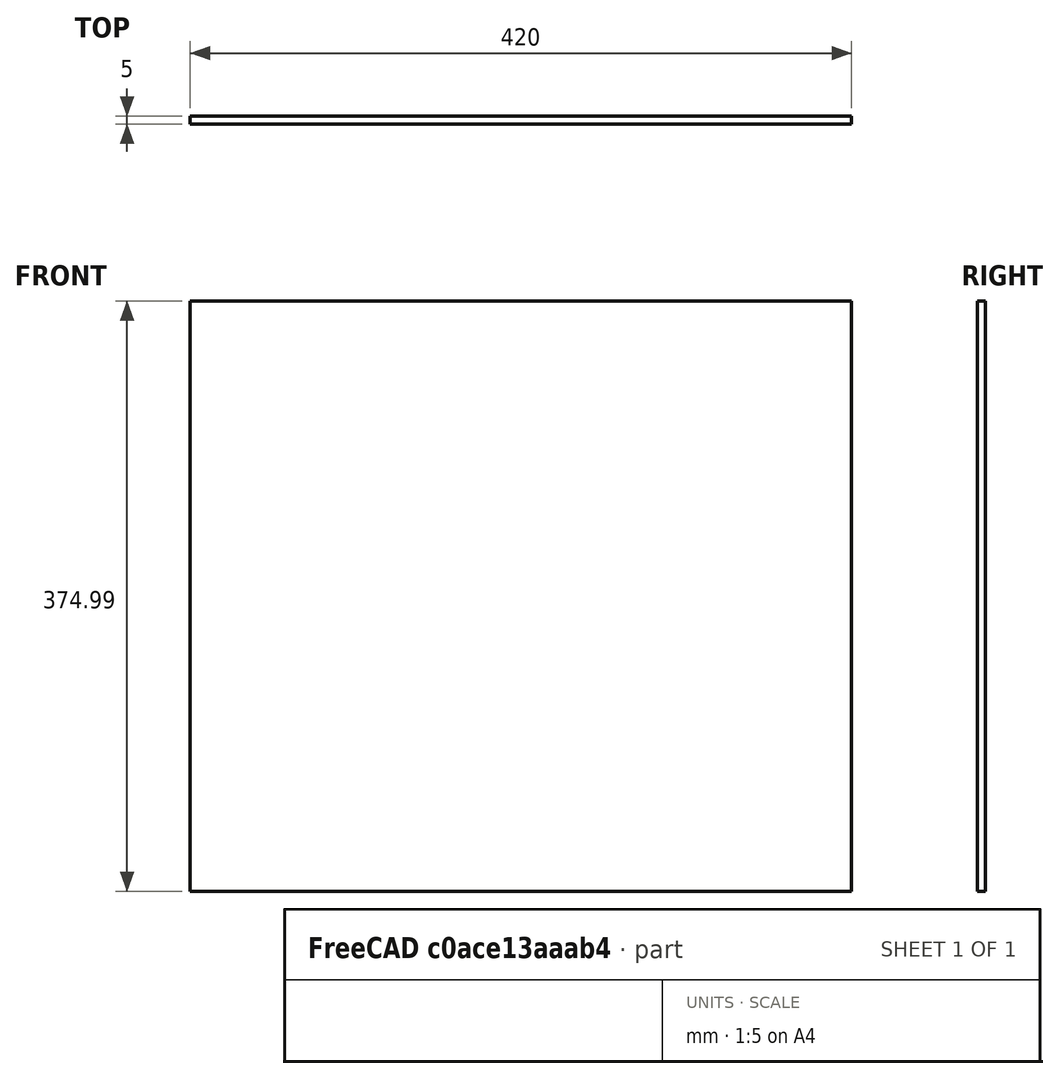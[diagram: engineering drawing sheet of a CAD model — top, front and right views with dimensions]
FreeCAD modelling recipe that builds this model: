
FCSTD DOCUMENT  (FreeCAD 0.16R6706 (Git))
Label: upper_plate
License: All rights reserved
LicenseURL: http://en.wikipedia.org/wiki/All_rights_reserved
objects: Sketcher::SketchObject×1, PartDesign::Pad×1, Part::Feature×1
note: 4 computed .brp shape members not serialized (recipe doc carries the construction recipe); baked Part::Feature solids carry a one-line shape summary decoded from their .brp

FEATURE [Sketcher::SketchObject] Sketch
  Placement = pos=(0,0,0) rot=(1,0,0;1.5708rad)
  sketch-geometry (4):
    g0: LineSegment StartX=0 StartY=0 StartZ=0 EndX=420 EndY=0 EndZ=0
    g1: LineSegment StartX=420 StartY=0 StartZ=0 EndX=420 EndY=374.99 EndZ=0
    g2: LineSegment StartX=420 StartY=374.99 StartZ=0 EndX=0 EndY=374.99 EndZ=0
    g3: LineSegment StartX=0 StartY=374.99 StartZ=0 EndX=0 EndY=0 EndZ=0
  constraints (11):
    c: Coincident(g0,g1)
    c: Coincident(g1,g2)
    c: Coincident(g2,g3)
    c: Coincident(g3,g0)
    c: Horizontal(g0)
    c: Horizontal(g2)
    c: Vertical(g1)
    c: Vertical(g3)
    c: Coincident(g0,g-1)
    c: DistanceY(g1,g1) = 374.99
    c: DistanceX(g0,g0) = 420
FEATURE [PartDesign::Pad] Pad
  Length = 5
  Length2 = 100
  Placement = pos=(0,0,0) rot=(1,0,0;1.5708rad)
  Sketch = -> Sketch
  Type = 0
FEATURE [Part::Feature] Pad001
  Placement = pos=(0,0,0) rot=(1,0,0;1.5708rad)
  shape: bbox 420 x 5 x 375 mm, 6 faces (baked)
